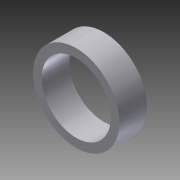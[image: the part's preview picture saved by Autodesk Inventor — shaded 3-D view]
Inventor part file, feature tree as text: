
AUTODESK INVENTOR PART (.ipt)
format: ipt  version: 2013 (Build 170138000, 138)  size: 82,944 bytes
history: native  units: in
note: dims shown in document units (in); Inventor stores cm internally (conversion verified against a paired STEP export)
features: extrude x1, sketch x1
ambient origin geometry x8: Origin, YZ Plane, XZ Plane, XY Plane, X Axis, Y Axis, Z Axis, Center Point
bodies: Solid1 (feature_tree)
feature tree (2):
  extrude  "Extrusion1"  Depth=0.5in
  sketch  "Sketch1"  dims[d0=0.625in d1=0.5in d2=0.2in d3=0.0in]
